# Revit family: deepliner 76×2000×4_WBQ LP76×2000×4
name_source: partatom
category: Generic Models
units: mm (PartAtom-declared; Revit-internal decimal feet)

## family parameters
Always vertical = Yes
Can host rebar = No
Cut with Voids When Loaded = Yes
Maintain Annotation Orientation = No
Part Type = Normal
Room Calculation Point = No
Round Connector Dimension = Use Diameter
Shared = No
Work Plane-Based = No

## types (1)
- deepliner 76×2000×4_WBQ LP76×2000×4
    Default Elevation = 0 mm  [stored 0 ft]
    Description = Screws
    Head = Yes
    Length = 2000 mm  [stored 6.56168 ft]
    Load capacity = (vertical, Pull-out, Horizontal-Indicative only)
    Manufacturer = ROCKBASE
    Material Specs = S355B
    Model = WBQ LP76×2000×4
WBQ LP76×2000×4
WBQ LP76×2000×4
    Outer diameter = 76 mm  [stored 0.249344 ft]
    Spiral Pitch = 2 mm  [stored 0.00656168 ft]
    Type Image = LOGO ROCKB.jpeg
    URL = https://www.rockbase.co.il
    Wall Thikness = 4 mm  [stored 0.0131234 ft]

note: [stored X ft] marks values corroborated as IEEE doubles in the binary element streams (Revit-internal decimal feet)

## geometry (parser evidence)
native form markers: Sweep x9
no freeform markers — native parametric forms only
